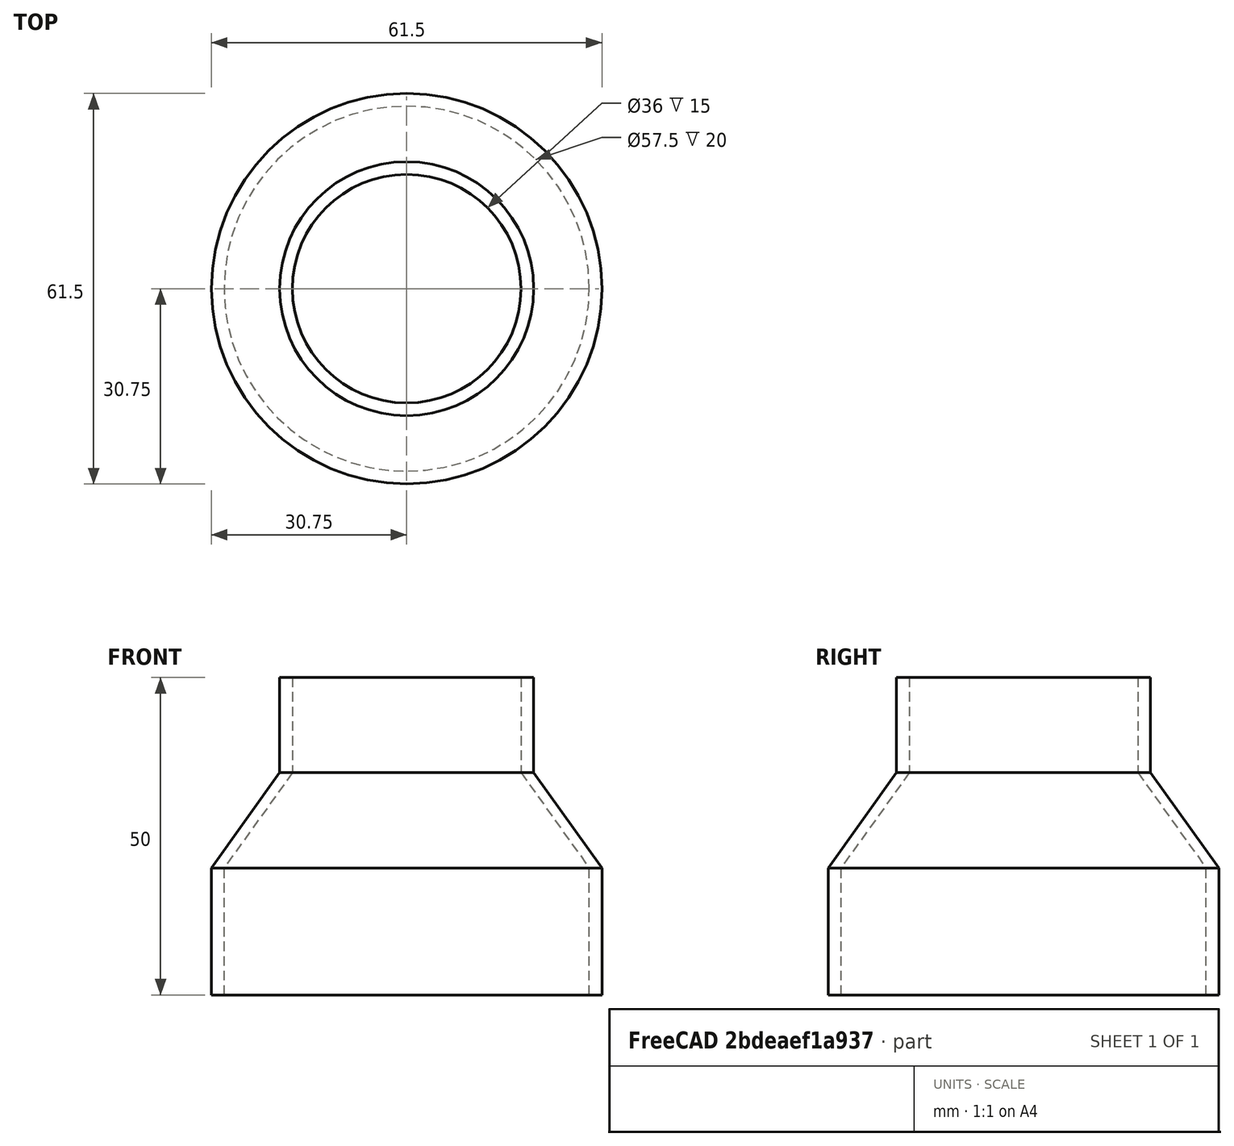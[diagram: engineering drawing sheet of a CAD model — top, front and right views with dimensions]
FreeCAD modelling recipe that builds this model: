
FCSTD DOCUMENT  (FreeCAD 0.21RUnknown)
Label: shop-vac-adapter
License: All rights reserved
LicenseURL: http://en.wikipedia.org/wiki/All_rights_reserved
objects: Spreadsheet::Sheet×1, Sketcher::SketchObject×1, PartDesign::Revolution×1, PartDesign::Body×1
note: 4 computed .brp shape members not serialized (recipe doc carries the construction recipe); baked Part::Feature solids carry a one-line shape summary decoded from their .brp

FEATURE [Spreadsheet::Sheet] Spreadsheet
  Configuration = 1
  cells = B1='ToolOD; C1='VacOD; D1='ToolWallThickness; E1='VacWallThickness; F1='ToolNozzleHeight; G1='VacNozzleHeight; H1='NozzleReductionLength; A2==hiddenref(Body.Configuration.String); B2(ToolOD)==.B5; C2(VacOD)==.C5; D2(ToolWallThickness)==.D5; E2(VacWallThickness)==.E5; F2(ToolNozzleHeight)==.F5; G2(VacNozzleHeight)==.G5; H2(NozzleReductionLength)==.H5; A3='default; B3=10; C3=15; D3=2; E3=2; F3=15; G3=15; H3=15; A4='HercMiter-BauerVac; B4==46.7 - 4; C4=57.5; D4=2; E4=2; F4=15; G4=20; H4=15; A5='HercCirc-BauerVac; B5=36; C5=57.5; D5=2; E5=2; F5=15; G5=20; H5=15
  expr: .Configuration.Enum = cells[<<A3:|>>]
  expr: .cells.Bind.B2.ZZ2 = tuple(.cells; <<B>> + str(hiddenref(Body.Configuration) + 3); <<ZZ>> + str(hiddenref(Body.Configuration) + 3))
FEATURE [Sketcher::SketchObject] Sketch
  FullyConstrained = true
  MapMode = 5
  Placement = pos=(0,0,0) rot=(1,0,0;1.5708rad)
  Support = -> [XZ_Plane]
  expr: Constraints[17] = Spreadsheet.ToolWallThickness
  expr: Constraints[18] = Spreadsheet.VacWallThickness
  expr: Constraints[19] = Spreadsheet.VacOD / 2
  expr: Constraints[20] = Spreadsheet.ToolOD / 2
  expr: Constraints[21] = Spreadsheet.ToolNozzleHeight
  expr: Constraints[22] = Spreadsheet.VacNozzleHeight
  expr: Constraints[23] = Spreadsheet.NozzleReductionLength
  sketch-geometry (8):
    g0: LineSegment StartX=28.75 StartY=0 StartZ=0 EndX=30.75 EndY=0 EndZ=0
    g1: LineSegment StartX=30.75 StartY=20 StartZ=0 EndX=30.75 EndY=0 EndZ=0
    g2: LineSegment StartX=18 StartY=50 StartZ=0 EndX=18 EndY=35 EndZ=0
    g3: LineSegment StartX=18 StartY=50 StartZ=0 EndX=20 EndY=50 EndZ=0
    g4: LineSegment StartX=20 StartY=50 StartZ=0 EndX=20 EndY=35 EndZ=0
    g5: LineSegment StartX=28.75 StartY=0 StartZ=0 EndX=28.75 EndY=20 EndZ=0
    g6: LineSegment StartX=18 StartY=35 StartZ=0 EndX=28.75 EndY=20 EndZ=0
    g7: LineSegment StartX=20 StartY=35 StartZ=0 EndX=30.75 EndY=20 EndZ=0
  constraints (24):
    c: PointOnObject(g0,g-1)
    c: Coincident(g1,g0)
    c: Vertical(g1)
    c: Vertical(g2)
    c: Coincident(g3,g2)
    c: Horizontal(g3)
    c: Vertical(g4)
    c: Coincident(g3,g4)
    c: Vertical(g5)
    c: Coincident(g0,g5)
    c: Coincident(g2,g6)
    c: Coincident(g6,g5)
    c: Coincident(g7,g4)
    c: Coincident(g1,g7)
    c: Parallel(g6,g7)
    c: Horizontal(g2,g4)
    c: Horizontal(g0)
    c: DistanceX(g3,g3) = 2
    c: DistanceX(g0,g0) = 2
    c: DistanceX(g-1,g0) = 28.75
    c: DistanceX(g-1,g2) = 18
    c: DistanceY(g4,g4) = 15
    c: DistanceY(g1,g1) = 20
    c: DistanceY(g1,g4) = 15
FEATURE [PartDesign::Revolution] Revolution
  Angle = 360
  Axis = (0,-2e-16,1)
  Base = (0,0,0)
  Placement = pos=(0,0,0) rot=(1,0,0;1.5708rad)
  Profile = -> Sketch
  ReferenceAxis = -> Sketch [V_Axis]
  Reversed = true
FEATURE [PartDesign::Body] Body
  Configruation = 1
  Configuration = 2
  Group = -> [Sketch,Revolution]
  Origin = -> Origin
  Tip = -> Revolution
  expr: .Configruation.Enum = Spreadsheet.cells[<<A3:|>>]
  expr: .Configuration.Enum = Spreadsheet.cells[<<A3:|>>]
